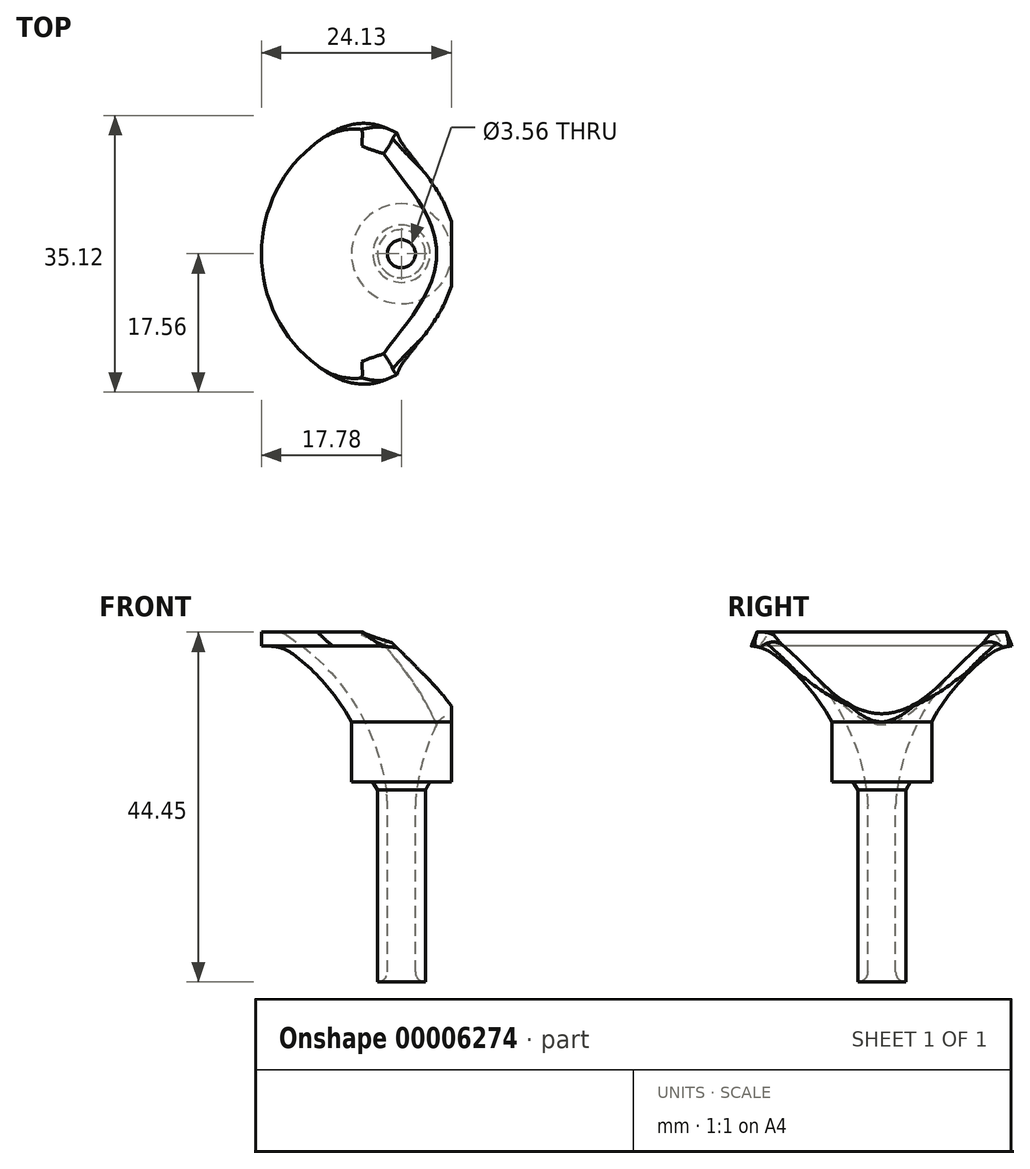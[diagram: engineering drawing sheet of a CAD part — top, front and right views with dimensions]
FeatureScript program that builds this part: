
annotation { "Feature Type Name" : "Feature", "Feature Type Description" : "" }
export const myFeature = defineFeature(function(context is Context, id is Id, definition is map)
    precondition{}
    {
        {
            var Q0;
            Q0=qCreatedBy(makeId("Right.planeOp"),FACE);
            var sketch = newSketch(context, id + "F0", { "sketchPlane" : qUnion([Q0])});
            skLineSegment(sketch, "E0", {"start": v(6.35, 7.65) * mm, "end": v(6.35, 0) * mm});
            skLineSegment(sketch, "E1", {"start": v(6.35, 0) * mm, "end": v(3.63, 0) * mm});
            skLineSegment(sketch, "E2", {"start": v(3.63, 0) * mm, "end": v(3.05, -1.02) * mm});
            skLineSegment(sketch, "E3", {"start": v(3.05, -1.02) * mm, "end": v(3.05, -25.4) * mm});
            skLineSegment(sketch, "E4", {"start": v(3.05, -25.4) * mm, "end": v(1.78, -25.4) * mm});
            skLineSegment(sketch, "E5", {"start": v(1.78, -25.4) * mm, "end": v(1.78, -2.4) * mm});
            skLineSegment(sketch, "E6", {"start": v(0, 2.83) * mm, "end": v(0, -5.35) * mm, "construction": true});
            skLineSegment(sketch, "E7", {"start": v(15.24, 19.05) * mm, "end": v(17.78, 19.05) * mm});
            skLineSegment(sketch, "E8", {"start": v(15.24, 17.27) * mm, "end": v(17.78, 17.27) * mm});
            skLineSegment(sketch, "E9", {"start": v(17.78, 17.27) * mm, "end": v(17.78, 19.05) * mm});
            skArc(sketch, "E10", {"start": v(15.24, 19.05) * mm, "mid": v(5.94, 9.94) * mm, "end": v(1.78, -2.4) * mm});
            skArc(sketch, "E11.0", {"start": v(15.24, 17.27) * mm, "mid": v(10.19, 13.02) * mm, "end": v(6.35, 7.65) * mm});
            skLineSegment(sketch, "E12", {"start": v(0, 0) * mm, "end": v(-3.33, 0) * mm, "construction": true});
            skSolve(sketch);
        }
        {
            var Q0;
            Q0 = qSketchRegion(id + "F0", true);
            var Q1;
            Q1=sQuery(id+"F0.wireOp",EDGE,"E6");
            revolve(context, id + "F1", {"entities" : qUnion([Q0]), "axis" : qUnion([Q1]), "revolveType" : RevolveType.FULL});
        }
        {
            var Q0;
            Q0=makeQuery(id+"F1.opRevolve","SWEPT_EDGE",EDGE,{"disambiguationData":[OSD([sQuery(id+"F0.wireOp",EDGE,"E4"),sQuery(id+"F0.wireOp",EDGE,"E5")])]});
            fillet(context, id + "F2", {"entities" : qUnion([Q0]), "radius" : 1.27 * mm, "tangentPropagation" : true, "allowEdgeOverflow" : false});
        }
        {
            var Q0;
            Q0=makeQuery(id+"F1.opRevolve","SWEPT_FACE",FACE,{"disambiguationData":[OSD([sQuery(id+"F0.wireOp",EDGE,"E7")])]});
            var sketch = newSketch(context, id + "F3", { "sketchPlane" : qUnion([Q0])});
            skLineSegment(sketch, "E13", {"start": v(0, 0) * mm, "end": v(0, -27.09) * mm, "construction": true});
            skLineSegment(sketch, "E14", {"start": v(6.35, -16.6) * mm, "end": v(17.78, -16.6) * mm});
            skLineSegment(sketch, "E15", {"start": v(17.78, -16.6) * mm, "end": v(17.78, 16.6) * mm});
            skLineSegment(sketch, "E16", {"start": v(17.78, 16.6) * mm, "end": v(6.35, 16.6) * mm});
            skLineSegment(sketch, "E17", {"start": v(6.35, -16.6) * mm, "end": v(6.35, 16.6) * mm});
            skSolve(sketch);
        }
        {
            var Q0;
            Q0 = qSketchRegion(id + "F3", true);
            extrude(context, id + "F4", {"entities" : qUnion([Q0]), "operationType" : NewBodyOperationType.REMOVE, "endBound" : BoundingType.THROUGH_ALL, "oppositeDirection" : true, "depth" : 25.4 * mm});
        }
        {
            var Q0;
            Q0=makeQuery(id+"F1.opRevolve","SWEPT_EDGE",EDGE,{"disambiguationData":[OSD([sQuery(id+"F0.wireOp",EDGE,"E5"),sQuery(id+"F0.wireOp",EDGE,"E10")])]});
            fillet(context, id + "F5", {"entities" : qUnion([Q0]), "radius" : 12.7 * mm, "tangentPropagation" : true, "allowEdgeOverflow" : false});
        }
        {
            var Q0;
            Q0=qCreatedBy(makeId("Front.planeOp"),FACE);
            var sketch = newSketch(context, id + "F6", { "sketchPlane" : qUnion([Q0])});
            skLineSegment(sketch, "E18.0", {"start": v(-2.54, 19.05) * mm, "end": v(6.35, 19.05) * mm});
            skLineSegment(sketch, "E19.0", {"start": v(6.35, 17.27) * mm, "end": v(6.35, 19.05) * mm});
            skLineSegment(sketch, "E20", {"start": v(-2.54, 19.05) * mm, "end": v(6.35, 10.16) * mm});
            skLineSegment(sketch, "E21", {"start": v(6.35, 17.27) * mm, "end": v(6.35, 10.16) * mm});
            skPoint(sketch, "E22.orphan", {"position": v(-17.78, 19.05) * mm});
            skSolve(sketch);
        }
        {
            var Q0;
            Q0 = qSketchRegion(id + "F6", true);
            extrude(context, id + "F7", {"entities" : qUnion([Q0]), "operationType" : NewBodyOperationType.REMOVE, "endBound" : BoundingType.SYMMETRIC, "depth" : 63.5 * mm});
        }
        {
            var Q0;
            Q0=makeQuery(id+"F7.boolean.opBoolean","INTERSECT",EDGE,{"disambiguationData":[OD(1.0)],"derivedFrom":[makeQuery(id+"F1.opRevolve","SWEPT_FACE",FACE,{"disambiguationData":[OSD([sQuery(id+"F0.wireOp",EDGE,"E9")])]}),makeQuery(id+"F7.opExtrude","SWEPT_FACE",FACE,{"disambiguationData":[OSD([sQuery(id+"F6.wireOp",EDGE,"E20")])]})]});
            var Q1;
            Q1=makeQuery(id+"F7.boolean.opBoolean","INTERSECT",EDGE,{"disambiguationData":[OD(0.0)],"derivedFrom":[makeQuery(id+"F1.opRevolve","SWEPT_FACE",FACE,{"disambiguationData":[OSD([sQuery(id+"F0.wireOp",EDGE,"E9")])]}),makeQuery(id+"F7.opExtrude","SWEPT_FACE",FACE,{"disambiguationData":[OSD([sQuery(id+"F6.wireOp",EDGE,"E20")])]})]});
            chamfer(context, id + "F8", {"entities" : qUnion([Q0, Q1]), "width" : 2.3 * mm, "tangentPropagation" : true});
        }
        {
            var Q0;
            Q0=makeQuery(id+"F7.boolean.opBoolean","COPY",EDGE,{"disambiguationData":[OD(0.0)],"derivedFrom":makeQuery(id+"F7.opExtrude","SWEPT_EDGE",EDGE,{"disambiguationData":[OSD([sQuery(id+"F6.wireOp",EDGE,"E20"),sQuery(id+"F6.wireOp",EDGE,"E21")])]})});
            var Q1;
            Q1=makeQuery(id+"F7.boolean.opBoolean","COPY",EDGE,{"disambiguationData":[OD(0.0)],"derivedFrom":makeQuery(id+"F7.opExtrude","SWEPT_EDGE",EDGE,{"disambiguationData":[OSD([sQuery(id+"F6.wireOp",EDGE,"E18.0"),sQuery(id+"F6.wireOp",EDGE,"E20")])]})});
            var Q2;
            Q2=makeQuery(id+"F7.boolean.opBoolean","COPY",EDGE,{"disambiguationData":[OD(1.0)],"derivedFrom":makeQuery(id+"F7.opExtrude","SWEPT_EDGE",EDGE,{"disambiguationData":[OSD([sQuery(id+"F6.wireOp",EDGE,"E18.0"),sQuery(id+"F6.wireOp",EDGE,"E20")])]})});
            var Q3;
            Q3=makeQuery(id+"F1.opRevolve","SWEPT_EDGE",EDGE,{"disambiguationData":[OSD([sQuery(id+"F0.wireOp",EDGE,"E8"),sQuery(id+"F0.wireOp",EDGE,"E11.0")])]});
            var Q4;
            {var subQ0=makeQuery(id+"F1.opRevolve","SWEPT_FACE",FACE,{"disambiguationData":[OSD([sQuery(id+"F0.wireOp",EDGE,"E9")])]});Q4=makeQuery(id+"F8.opChamfer","BLEND_EDGE",EDGE,{"blendedFrom":[makeQuery(id+"F7.boolean.opBoolean","INTERSECT",EDGE,{"disambiguationData":[OD(0.0)],"derivedFrom":[subQ0,makeQuery(id+"F7.opExtrude","SWEPT_FACE",FACE,{"disambiguationData":[OSD([sQuery(id+"F6.wireOp",EDGE,"E20")])]})]}),subQ0],"blendedInto":[subQ0]});}
            var Q5;
            {var subQ0=makeQuery(id+"F1.opRevolve","SWEPT_FACE",FACE,{"disambiguationData":[OSD([sQuery(id+"F0.wireOp",EDGE,"E9")])]});Q5=makeQuery(id+"F8.opChamfer","BLEND_EDGE",EDGE,{"blendedFrom":[makeQuery(id+"F7.boolean.opBoolean","INTERSECT",EDGE,{"disambiguationData":[OD(1.0)],"derivedFrom":[subQ0,makeQuery(id+"F7.opExtrude","SWEPT_FACE",FACE,{"disambiguationData":[OSD([sQuery(id+"F6.wireOp",EDGE,"E20")])]})]}),subQ0],"blendedInto":[subQ0]});}
            fillet(context, id + "F9", {"entities" : qUnion([Q0, Q1, Q2, Q3, Q4, Q5]), "radius" : 5.08 * mm, "tangentPropagation" : true, "allowEdgeOverflow" : false});
        }
        {
            var Q0;
            Q0=makeQuery(id+"F1.opRevolve","SWEPT_FACE",FACE,{"disambiguationData":[OSD([sQuery(id+"F0.wireOp",EDGE,"E10")])]});
            fillet(context, id + "F10", {"entities" : qUnion([Q0]), "radius" : 2.54 * mm, "tangentPropagation" : true, "allowEdgeOverflow" : false});
        }
    });
